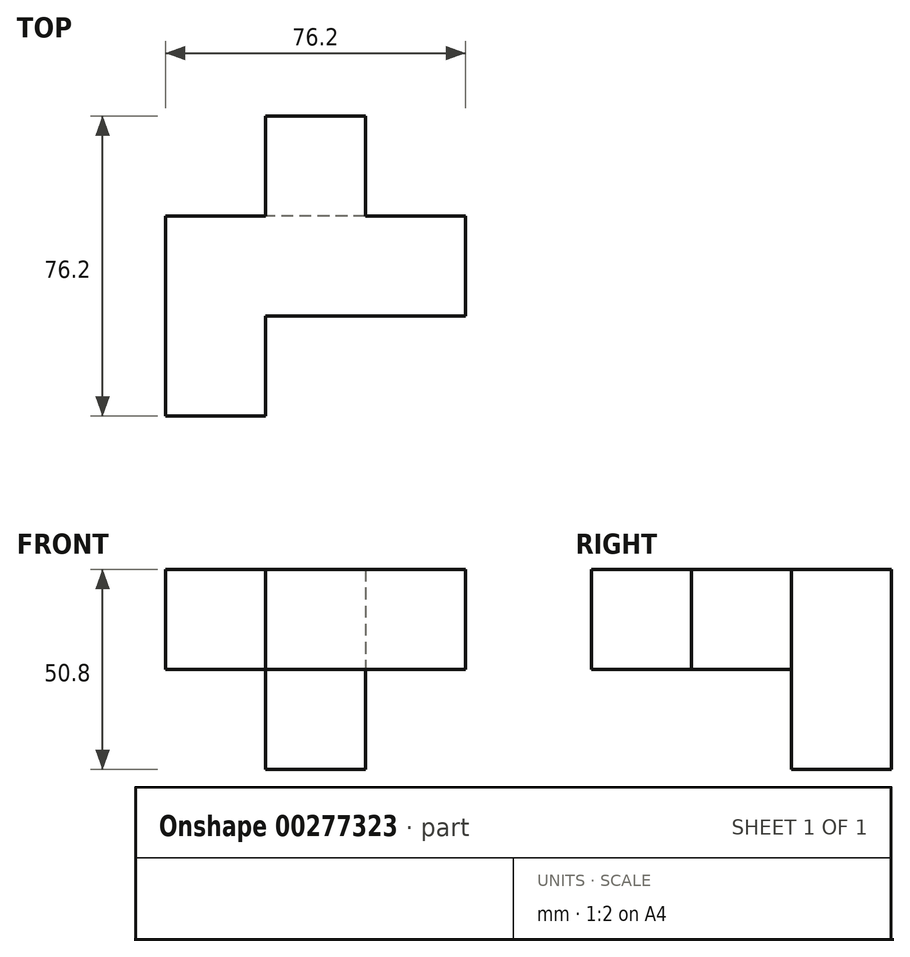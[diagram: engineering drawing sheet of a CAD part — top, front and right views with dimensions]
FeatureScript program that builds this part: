
annotation { "Feature Type Name" : "Feature", "Feature Type Description" : "" }
export const myFeature = defineFeature(function(context is Context, id is Id, definition is map)
    precondition{}
    {
        {
            var Q0;
            Q0=qCreatedBy(makeId("Front.planeOp"),FACE);
            var sketch = newSketch(context, id + "F0", { "sketchPlane" : qUnion([Q0])});
            skLineSegment(sketch, "E0.bottom", {"start": v(-46.96, -24.15) * mm, "end": v(-72.36, -24.15) * mm});
            skLineSegment(sketch, "E0.top", {"start": v(-46.96, 1.25) * mm, "end": v(-72.36, 1.25) * mm});
            skLineSegment(sketch, "E0.left", {"start": v(-46.96, -24.15) * mm, "end": v(-46.96, 1.25) * mm});
            skLineSegment(sketch, "E0.right", {"start": v(-72.36, -24.15) * mm, "end": v(-72.36, 1.25) * mm});
            skPoint(sketch, "E0.middle", {"position": v(-59.66, -11.45) * mm});
            skSolve(sketch);
        }
        {
            var Q0;
            Q0 = qSketchRegion(id + "F0", true);
            extrude(context, id + "F1", {"entities" : qUnion([Q0]), "depth" : 50.8 * mm});
        }
        {
            var Q0;
            Q0=makeQuery(id+"F1.opExtrude","SWEPT_FACE",FACE,{"disambiguationData":[OSD([sQuery(id+"F0.wireOp",EDGE,"E0.left")])]});
            var sketch = newSketch(context, id + "F2", { "sketchPlane" : qUnion([Q0])});
            skLineSegment(sketch, "E1.bottom", {"start": v(0, -24.15) * mm, "end": v(-25.4, -24.15) * mm});
            skLineSegment(sketch, "E1.top", {"start": v(0, 1.25) * mm, "end": v(-25.4, 1.25) * mm});
            skLineSegment(sketch, "E1.left", {"start": v(0, -24.15) * mm, "end": v(0, 1.25) * mm});
            skLineSegment(sketch, "E1.right", {"start": v(-25.4, -24.15) * mm, "end": v(-25.4, 1.25) * mm});
            skSolve(sketch);
        }
        {
            var Q0;
            Q0 = qSketchRegion(id + "F2", true);
            extrude(context, id + "F3", {"entities" : qUnion([Q0]), "operationType" : NewBodyOperationType.ADD, "depth" : 50.8 * mm});
        }
        {
            var Q0;
            Q0=makeQuery(id+"F3.opExtrude","SWEPT_FACE",FACE,{"disambiguationData":[OSD([sQuery(id+"F2.wireOp",EDGE,"E1.right")])]});
            var sketch = newSketch(context, id + "F4", { "sketchPlane" : qUnion([Q0])});
            skLineSegment(sketch, "E2.bottom", {"start": v(-46.96, 1.25) * mm, "end": v(-21.56, 1.25) * mm});
            skLineSegment(sketch, "E2.top", {"start": v(-46.96, -24.15) * mm, "end": v(-21.56, -24.15) * mm});
            skLineSegment(sketch, "E2.left", {"start": v(-46.96, 1.25) * mm, "end": v(-46.96, -24.15) * mm});
            skLineSegment(sketch, "E2.right", {"start": v(-21.56, 1.25) * mm, "end": v(-21.56, -24.15) * mm});
            skSolve(sketch);
        }
        {
            var Q0;
            Q0 = qSketchRegion(id + "F4", true);
            extrude(context, id + "F5", {"entities" : qUnion([Q0]), "operationType" : NewBodyOperationType.ADD, "oppositeDirection" : true, "depth" : 50.8 * mm});
        }
        {
            var Q0;
            Q0=makeQuery(id+"F5.boolean.opBoolean","MERGE",FACE,{"derivedFrom":[makeQuery(id+"F3.boolean.opBoolean","MERGE",FACE,{"derivedFrom":[makeQuery(id+"F1.opExtrude","SWEPT_FACE",FACE,{"disambiguationData":[OSD([sQuery(id+"F0.wireOp",EDGE,"E0.bottom")])]}),makeQuery(id+"F3.opExtrude","SWEPT_FACE",FACE,{"disambiguationData":[OSD([sQuery(id+"F2.wireOp",EDGE,"E1.bottom")])]})]}),makeQuery(id+"F5.opExtrude","SWEPT_FACE",FACE,{"disambiguationData":[OSD([sQuery(id+"F4.wireOp",EDGE,"E2.top")])]})]});
            var sketch = newSketch(context, id + "F6", { "sketchPlane" : qUnion([Q0])});
            skLineSegment(sketch, "E3.bottom", {"start": v(-21.56, -25.4) * mm, "end": v(-46.96, -25.4) * mm});
            skLineSegment(sketch, "E3.top", {"start": v(-21.56, 0) * mm, "end": v(-46.96, 0) * mm});
            skLineSegment(sketch, "E3.left", {"start": v(-21.56, -25.4) * mm, "end": v(-21.56, 0) * mm});
            skLineSegment(sketch, "E3.right", {"start": v(-46.96, -25.4) * mm, "end": v(-46.96, 0) * mm});
            skSolve(sketch);
        }
        {
            var Q0;
            Q0 = qSketchRegion(id + "F6", true);
            extrude(context, id + "F7", {"entities" : qUnion([Q0]), "operationType" : NewBodyOperationType.ADD, "depth" : 25.4 * mm});
        }
    });
